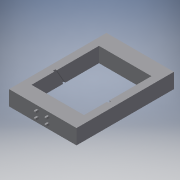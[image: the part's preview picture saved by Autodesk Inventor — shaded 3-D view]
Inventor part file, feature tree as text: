
AUTODESK INVENTOR PART (.ipt)
format: ipt  version: 2018.3 (Build 223284000, 284)  size: 232,960 bytes
history: native  units: mm
features: extrude x5, sketch x5, chamfer x2
ambient origin geometry x8: Origin, YZ Plane, XZ Plane, XY Plane, X Axis, Y Axis, Z Axis, Center Point
bodies: Solid1 (feature_tree)
feature tree (12):
  extrude  "Extrusion1"  Depth=130.0mm
  extrude  "Extrusion2"  Depth=90.0mm
  extrude  "Extrusion3"  TaperAngle=210.0deg  [1 undecoded]
  extrude  "Extrusion4"  Depth=2.0mm
  chamfer  "Chamfer1"  Distance=2.0mm
  extrude  "Extrusion5"  Depth=2.0mm
  chamfer  "Chamfer2"  Distance=26.471143mm
  sketch  "Sketch1"  dims[d0=90.0mm d1=130.0mm]
  sketch  "Sketch2"  dims[d2=70.0mm d3=90.0mm]
  sketch  "Sketch3"  dims[d4=20.0mm d5=0.0mm d6=210.0deg]
  sketch  "Sketch4"  dims[d7=3.0mm d8=26.471143mm d9=2.0mm d10=0.0mm]
  sketch  "Sketch5"  dims[d11=30.0deg d12=3.0mm d13=26.471143mm d14=2.0mm d15=0.0mm d16=20.0mm d17=20.0mm d18=10.0mm d19=20.0mm d20=14.0mm d21=3.0mm d22=3.0mm d23=35.0mm d24=35.0mm d25=1.45mm d26=1.45mm d27=1.1mm d28=1.1mm d29=12.11mm d30=1.13mm d31=1.13mm d32=4.83mm d33=4.83mm d34=1.129mm d35=1.128692mm d36=4.0mm d37=0.0mm d38=0.5mm d39=2.0mm d40=45.0deg d41=20.0mm d42=14.0mm d43=3.0mm d44=3.0mm d45=35.0mm d46=35.0mm d62=2.15mm d63=2.15mm d64=2.15mm d65=2.15mm d66=1.13mm d67=1.13mm d68=1.128mm d69=1.1mm d70=1.1mm d71=1.45mm d72=1.45mm d73=1.128mm d74=4.0mm d75=0.0mm d76=0.5mm d77=2.0mm d78=45.0deg]
note: 1 required parameter value undecoded (feature->parameter linkage not recoverable at this tier; creation-order binding heuristic only, values carry confidence <= 0.55)
